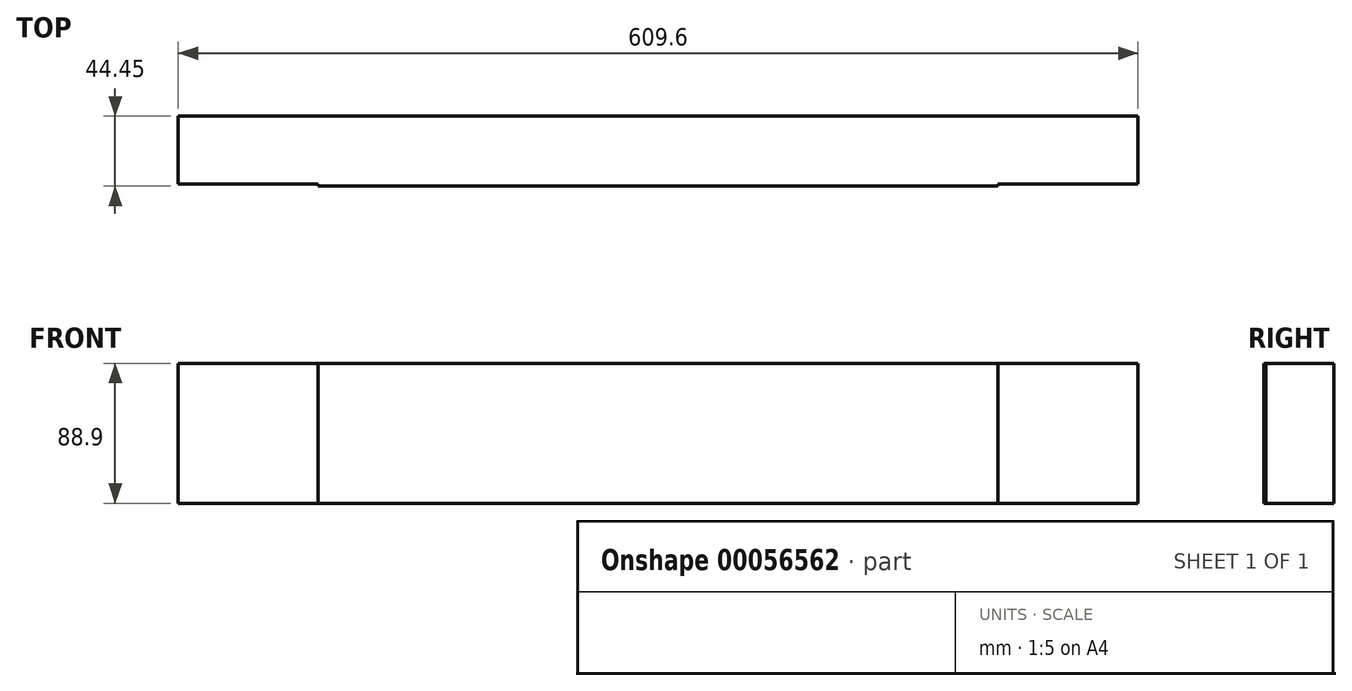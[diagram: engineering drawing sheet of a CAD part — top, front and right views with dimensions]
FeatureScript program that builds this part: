
annotation { "Feature Type Name" : "Feature", "Feature Type Description" : "" }
export const myFeature = defineFeature(function(context is Context, id is Id, definition is map)
    precondition{}
    {
        {
            var Q0;
            Q0=qCreatedBy(makeId("Front.planeOp"),FACE);
            var sketch = newSketch(context, id + "F0", { "sketchPlane" : qUnion([Q0])});
            skLineSegment(sketch, "E0.bottom", {"start": v(0, 0) * mm, "end": v(-609.6, 0) * mm});
            skLineSegment(sketch, "E0.top", {"start": v(0, 88.9) * mm, "end": v(-609.6, 88.9) * mm});
            skLineSegment(sketch, "E0.left", {"start": v(0, 0) * mm, "end": v(0, 88.9) * mm});
            skLineSegment(sketch, "E0.right", {"start": v(-609.6, 0) * mm, "end": v(-609.6, 88.9) * mm});
            skSolve(sketch);
        }
        {
            var Q0;
            Q0=makeQuery(id+"F0.imprint","IMPRINT",FACE,{"disambiguationData":[TD([[makeQuery(id+"F0.imprint","IMPRINT",EDGE,{"derivedFrom":sQuery(id+"F0.wireOp",EDGE,"E0.bottom")}),-1.0]])]});
            extrude(context, id + "F1", {"entities" : qUnion([Q0]), "depth" : 44.45 * mm});
        }
        {
            var Q0;
            Q0=makeQuery(id+"F1.opExtrude","CAP_FACE",FACE,{"disambiguationData":[OSD([sQuery(id+"F0.wireOp",EDGE,"E0.bottom"),sQuery(id+"F0.wireOp",EDGE,"E0.top"),sQuery(id+"F0.wireOp",EDGE,"E0.left"),sQuery(id+"F0.wireOp",EDGE,"E0.right")])],"isStart":false});
            var sketch = newSketch(context, id + "F2", { "sketchPlane" : qUnion([Q0])});
            skLineSegment(sketch, "E1.bottom", {"start": v(-609.6, 88.9) * mm, "end": v(-520.7, 88.9) * mm});
            skLineSegment(sketch, "E1.top", {"start": v(-609.6, 0) * mm, "end": v(-520.7, 0) * mm});
            skLineSegment(sketch, "E1.left", {"start": v(-609.6, 88.9) * mm, "end": v(-609.6, 0) * mm});
            skLineSegment(sketch, "E1.right", {"start": v(-520.7, 88.9) * mm, "end": v(-520.7, 0) * mm});
            skLineSegment(sketch, "E2.bottom", {"start": v(0, 88.9) * mm, "end": v(-88.9, 88.9) * mm});
            skLineSegment(sketch, "E2.top", {"start": v(0, 0) * mm, "end": v(-88.9, 0) * mm});
            skLineSegment(sketch, "E2.left", {"start": v(0, 88.9) * mm, "end": v(0, 0) * mm});
            skLineSegment(sketch, "E2.right", {"start": v(-88.9, 88.9) * mm, "end": v(-88.9, 0) * mm});
            skSolve(sketch);
        }
        {
            var Q0;
            Q0=makeQuery(id+"F2.imprint","IMPRINT",FACE,{"disambiguationData":[TD([[makeQuery(id+"F2.imprint","IMPRINT",EDGE,{"derivedFrom":sQuery(id+"F2.wireOp",EDGE,"E1.bottom")}),1.0]])]});
            extrude(context, id + "F3", {"entities" : qUnion([Q0]), "operationType" : NewBodyOperationType.REMOVE, "oppositeDirection" : true, "depth" : 1.27 * mm});
        }
        {
            var Q0;
            Q0=makeQuery(id+"F2.imprint","IMPRINT",FACE,{"disambiguationData":[TD([[makeQuery(id+"F2.imprint","IMPRINT",EDGE,{"derivedFrom":sQuery(id+"F2.wireOp",EDGE,"E2.bottom")}),1.0]])]});
            extrude(context, id + "F4", {"entities" : qUnion([Q0]), "operationType" : NewBodyOperationType.REMOVE, "oppositeDirection" : true, "depth" : 1.27 * mm});
        }
    });
